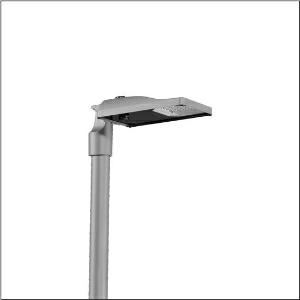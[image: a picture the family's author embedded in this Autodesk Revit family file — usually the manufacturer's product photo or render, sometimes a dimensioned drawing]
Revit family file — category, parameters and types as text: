
# Revit family: streetlight_sl_31_micro___st1_0a_5xh5d71t08da_8a50
name_source: partatom
category: Lighting Fixtures
units: mm (PartAtom-declared; Revit-internal decimal feet)

## family parameters
Cut with Voids When Loaded = No
Host = Face
Light Source = No
Part Type = Normal
Room Calculation Point = No
Round Connector Dimension = Use Diameter
Shared = No

## types (1)
- --- (1 x LED, 3990 lm, 37.7 W, 2200K)
    Apparent Load = 38 VA
    CIE Flux Codes = 37 72 97 100 100
    Color Rendering = 70
    Color Temperature = 2200K
    Default Elevation = 1800 mm
    Description = Streetlight SL 31 micro D4i, Desk-Remote mast luminaire for post-top, side-entry; light control with lens of PMMA; light distribution: ST1.0a, direct asymmetric distribution, for standard-compliant lighting for roads and squares; LED: luminous flux: 3.990lm, light colour: 722, colour temperature: 2200K; luminous efficacy: 105,8lm/W; control: pre-setting: logarithmic dimming characteristic, flexible luminous flux parameterisation, time-dependent luminous flux control, constant luminous flux control, power reduction, intelligent temperature release in ECG and LED module, overheat protection; luminaire housing, of diecast aluminium, SITECO metallic grey (DB 702S), corrosivity category C5 high according to DIN EN ISO 12944; cover of toughened safety glass, transparent, opened without tools; mast flange of diecast aluminium, SITECO metallic grey (DB 702S), spigot size: 76/60mm, mast flange included unmounted; cable length: 6,5m, connection cable pre-assembled; mains connection: 220..240V, AC, 50/60Hz; power consumption (at start of service life): 37,7W / (at end of service life): 40,9W / (with reduced operation 50%): 16,3W; protection rating (complete): IP66; insulation class (complete): insulation class II (safety insulation); impact resistance: IK09; certification: CE, ENEC, ENEC+, VDE, UKCA, ZD4i; permissible operating ambient temperature for outdoor applications: -40..+50°C; packaging unit: 1 piece

Light Distribution: ST1.0a
    Height = 76 mm
    Lamp = 1 x LED
    Lamp Light Flux = 3990 lm
    Lamp Power = 37.7 W
    Lamp count = 1
    Length = 467 mm
    Luminous efficacy = 106 lm/W
    Manufacturer = Siteco
    ModVariant = No
    Model = 5XH5D71T08DA
    Mounting Place = Pole
    Mounting Type = Pole top
    Number of Poles = 1
    OnlyDefault = Yes
    Power Factor = 1
    Product Name = Streetlight SL 31 micro | ST1.0a
    Product group = mast luminaire | pylon top
    ProductGroupID = 6100
    Protection Class = Protection class II
    Protection Degree = IP 66
    RLX_Detail_Level = 1
    RLX_Emergency_Light_Flux = 0 lm
    RLX_Emergency_Type = 0
    RLX_Emergency_Type_DB = No
    RlxData = <blob elided: 23369 chars, md5=d2aaf2ba>
    Socket = socket
    Standby Power = 0 W
    System Light Flux = 3990 lm
    System Power = 38 W
    Type Comments = factory setting: luminous flux: 100 % | dim-lin: 254 | 745 mA
    Type Image = l_1300315.jpg
    URL = http://relux.com
    VarID = @adj_010883
    Voltage = 0 V
    Weight = 0.00 kg
    Width = 265 mm

## geometry (parser evidence)
native form markers: Blend x4, Sweep x11
no freeform markers — native parametric forms only
